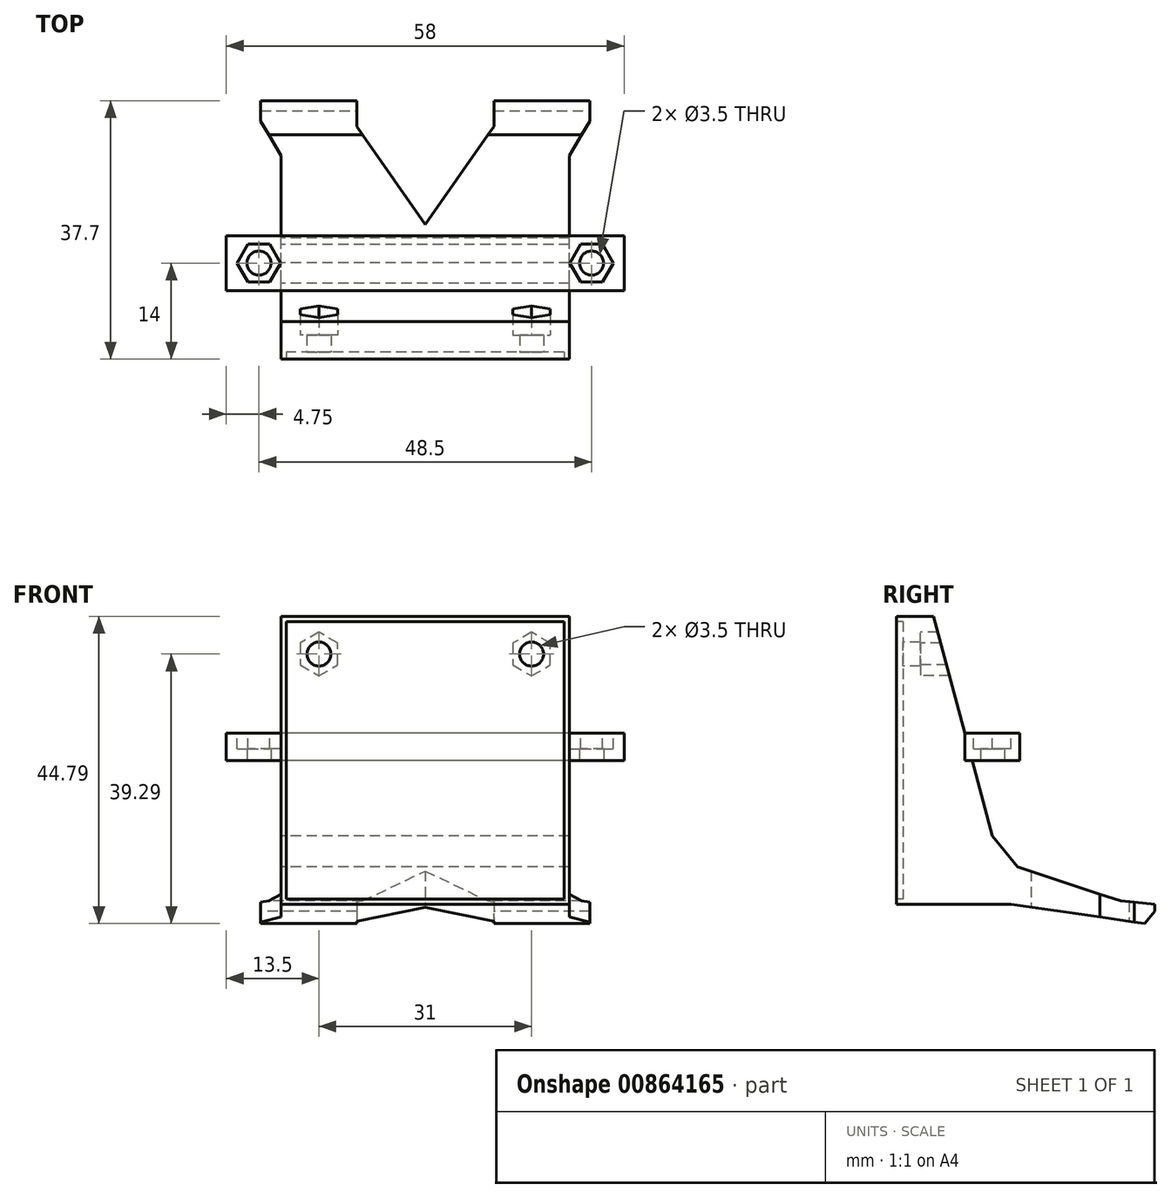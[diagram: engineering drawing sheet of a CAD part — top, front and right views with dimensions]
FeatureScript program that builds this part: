
annotation { "Feature Type Name" : "Feature", "Feature Type Description" : "" }
export const myFeature = defineFeature(function(context is Context, id is Id, definition is map)
    precondition{}
    {
        {
            var Q0;
            Q0=qCreatedBy(makeId("Top.planeOp"),FACE);
            var sketch = newSketch(context, id + "F0", { "sketchPlane" : qUnion([Q0])});
            skLineSegment(sketch, "E0", {"start": v(-24.25, 0) * mm, "end": v(0, 0) * mm, "construction": true});
            skLineSegment(sketch, "E1", {"start": v(0, 0) * mm, "end": v(24.25, 0) * mm, "construction": true});
            skCircle(sketch, "E2", {"center": v(-24.25, 0) * mm, "radius": 1.75 * mm});
            skCircle(sketch, "E3", {"center": v(24.25, 0) * mm, "radius": 1.75 * mm});
            skLineSegment(sketch, "E4.bottom", {"start": v(29, 4) * mm, "end": v(-29, 4) * mm});
            skLineSegment(sketch, "E4.top", {"start": v(29, -4) * mm, "end": v(-29, -4) * mm});
            skLineSegment(sketch, "E4.left", {"start": v(29, 4) * mm, "end": v(29, -4) * mm});
            skLineSegment(sketch, "E4.right", {"start": v(-29, 4) * mm, "end": v(-29, -4) * mm});
            skPoint(sketch, "E4.middle", {"position": v(0, 0) * mm});
            skSolve(sketch);
        }
        {
            var Q0;
            Q0 = qSketchRegion(id + "F0", true);
            extrude(context, id + "F1", {"entities" : qUnion([Q0]), "depth" : 4 * mm, "offsetDistance" : 25 * mm});
        }
        {
            var Q0;
            Q0=makeQuery(id+"F1.opExtrude","SWEPT_FACE",FACE,{"disambiguationData":[OSD([sQuery(id+"F0.wireOp",EDGE,"E4.top")])]});
            var sketch = newSketch(context, id + "F2", { "sketchPlane" : qUnion([Q0])});
            skLineSegment(sketch, "E5.bottom", {"start": v(21, 21) * mm, "end": v(-21, 21) * mm});
            skLineSegment(sketch, "E5.top", {"start": v(21, -21) * mm, "end": v(-21, -21) * mm});
            skLineSegment(sketch, "E5.left", {"start": v(21, 21) * mm, "end": v(21, -21) * mm});
            skLineSegment(sketch, "E5.right", {"start": v(-21, 21) * mm, "end": v(-21, -21) * mm});
            skLineSegment(sketch, "E6", {"start": v(-21, 0) * mm, "end": v(0, 0) * mm, "construction": true});
            skLineSegment(sketch, "E7", {"start": v(0, 0) * mm, "end": v(0, 21) * mm, "construction": true});
            skSolve(sketch);
        }
        {
            var Q0;
            Q0 = qSketchRegion(id + "F2", true);
            extrude(context, id + "F3", {"entities" : qUnion([Q0]), "operationType" : NewBodyOperationType.ADD, "depth" : 10 * mm, "offsetDistance" : 25 * mm});
        }
        {
            var Q0;
            Q0=makeQuery(id+"F1.opExtrude","CAP_FACE",FACE,{"disambiguationData":[OSD([sQuery(id+"F0.wireOp",EDGE,"E2"),sQuery(id+"F0.wireOp",EDGE,"E3"),sQuery(id+"F0.wireOp",EDGE,"E4.bottom"),sQuery(id+"F0.wireOp",EDGE,"E4.top"),sQuery(id+"F0.wireOp",EDGE,"E4.left"),sQuery(id+"F0.wireOp",EDGE,"E4.right")])],"isStart":false});
            var sketch = newSketch(context, id + "F4", { "sketchPlane" : qUnion([Q0])});
            skCircle(sketch, "E8.cCircle", {"center": v(24.25, 0) * mm, "radius": 2.75 * mm, "construction": true});
            skLineSegment(sketch, "E8.0", {"start": v(25.84, 2.75) * mm, "end": v(27.43, 0) * mm});
            skLineSegment(sketch, "E8.1", {"start": v(27.43, 0) * mm, "end": v(25.84, -2.75) * mm});
            skLineSegment(sketch, "E8.2", {"start": v(25.84, -2.75) * mm, "end": v(22.66, -2.75) * mm});
            skLineSegment(sketch, "E8.3", {"start": v(22.66, -2.75) * mm, "end": v(21.07, 0) * mm});
            skLineSegment(sketch, "E8.4", {"start": v(21.07, 0) * mm, "end": v(22.66, 2.75) * mm});
            skLineSegment(sketch, "E8.5", {"start": v(22.66, 2.75) * mm, "end": v(25.84, 2.75) * mm});
            skPoint(sketch, "E8.0.midPoint", {"position": v(26.63, 1.38) * mm});
            skCircle(sketch, "E9.cCircle", {"center": v(-24.25, 0) * mm, "radius": 2.75 * mm, "construction": true});
            skLineSegment(sketch, "E9.0", {"start": v(-21.07, 0) * mm, "end": v(-22.66, -2.75) * mm});
            skLineSegment(sketch, "E9.1", {"start": v(-22.66, -2.75) * mm, "end": v(-25.84, -2.75) * mm});
            skLineSegment(sketch, "E9.2", {"start": v(-25.84, -2.75) * mm, "end": v(-27.43, 0) * mm});
            skLineSegment(sketch, "E9.3", {"start": v(-27.43, 0) * mm, "end": v(-25.84, 2.75) * mm});
            skLineSegment(sketch, "E9.4", {"start": v(-25.84, 2.75) * mm, "end": v(-22.66, 2.75) * mm});
            skLineSegment(sketch, "E9.5", {"start": v(-22.66, 2.75) * mm, "end": v(-21.07, 0) * mm});
            skPoint(sketch, "E9.0.midPoint", {"position": v(-21.87, -1.38) * mm});
            skLineSegment(sketch, "E10", {"start": v(27.43, 0) * mm, "end": v(24.25, 0) * mm, "construction": true});
            skLineSegment(sketch, "E11", {"start": v(-21.07, 0) * mm, "end": v(-24.25, 0) * mm, "construction": true});
            skSolve(sketch);
        }
        {
            var Q0;
            Q0 = qSketchRegion(id + "F4", true);
            extrude(context, id + "F5", {"entities" : qUnion([Q0]), "operationType" : NewBodyOperationType.REMOVE, "oppositeDirection" : true, "depth" : 2.3 * mm, "offsetDistance" : 25 * mm});
        }
        {
            var Q0;
            Q0=makeQuery(id+"F3.opExtrude","SWEPT_FACE",FACE,{"disambiguationData":[OSD([sQuery(id+"F2.wireOp",EDGE,"E5.right")])]});
            var sketch = newSketch(context, id + "F6", { "sketchPlane" : qUnion([Q0])});
            skLineSegment(sketch, "E12", {"start": v(4, 21) * mm, "end": v(8.56, 21) * mm});
            skLineSegment(sketch, "E13", {"start": v(8.56, 21) * mm, "end": v(4, 4) * mm});
            skLineSegment(sketch, "E14", {"start": v(4, 4) * mm, "end": v(4, 21) * mm});
            skSolve(sketch);
        }
        {
            var Q0;
            Q0 = qSketchRegion(id + "F6", true);
            extrude(context, id + "F7", {"entities" : qUnion([Q0]), "operationType" : NewBodyOperationType.REMOVE, "endBound" : BoundingType.THROUGH_ALL, "oppositeDirection" : true, "depth" : 25 * mm, "offsetDistance" : 25 * mm});
        }
        {
            var Q0;
            Q0=makeQuery(id+"F3.opExtrude","SWEPT_FACE",FACE,{"disambiguationData":[OSD([sQuery(id+"F2.wireOp",EDGE,"E5.right")])]});
            var sketch = newSketch(context, id + "F8", { "sketchPlane" : qUnion([Q0])});
            skLineSegment(sketch, "E15", {"start": v(4, 0) * mm, "end": v(2.93, 0) * mm});
            skLineSegment(sketch, "E16", {"start": v(2.93, 0) * mm, "end": v(-2.7, -21) * mm});
            skLineSegment(sketch, "E17", {"start": v(-2.7, -21) * mm, "end": v(4, -21) * mm});
            skLineSegment(sketch, "E18", {"start": v(4, -21) * mm, "end": v(4, 0) * mm});
            skSolve(sketch);
        }
        {
            var Q0;
            Q0 = qSketchRegion(id + "F8", true);
            var Q1;
            Q1=makeQuery(id+"F3.opExtrude","SWEPT_FACE",FACE,{"disambiguationData":[OSD([sQuery(id+"F2.wireOp",EDGE,"E5.left")])]});
            extrude(context, id + "F9", {"entities" : qUnion([Q0]), "operationType" : NewBodyOperationType.ADD, "endBound" : BoundingType.UP_TO_SURFACE, "oppositeDirection" : true, "depth" : 25 * mm, "endBoundEntityFace" : qUnion([Q1]), "offsetDistance" : 25 * mm});
        }
        {
            var Q0;
            Q0=makeQuery(id+"F3.opExtrude","CAP_FACE",FACE,{"disambiguationData":[OSD([sQuery(id+"F2.wireOp",EDGE,"E5.bottom"),sQuery(id+"F2.wireOp",EDGE,"E5.top"),sQuery(id+"F2.wireOp",EDGE,"E5.left"),sQuery(id+"F2.wireOp",EDGE,"E5.right")])],"isStart":false});
            var sketch = newSketch(context, id + "F10", { "sketchPlane" : qUnion([Q0])});
            skLineSegment(sketch, "E19.bottom", {"start": v(15.5, -15.5) * mm, "end": v(-15.5, -15.5) * mm, "construction": true});
            skLineSegment(sketch, "E19.top", {"start": v(15.5, 15.5) * mm, "end": v(-15.5, 15.5) * mm, "construction": true});
            skLineSegment(sketch, "E19.left", {"start": v(15.5, -15.5) * mm, "end": v(15.5, 15.5) * mm, "construction": true});
            skLineSegment(sketch, "E19.right", {"start": v(-15.5, -15.5) * mm, "end": v(-15.5, 15.5) * mm, "construction": true});
            skPoint(sketch, "E19.middle", {"position": v(0, 0) * mm});
            skCircle(sketch, "E20", {"center": v(-15.5, 15.5) * mm, "radius": 1.75 * mm});
            skCircle(sketch, "E21", {"center": v(15.5, 15.5) * mm, "radius": 1.75 * mm});
            skSolve(sketch);
        }
        {
            var Q0;
            Q0 = qSketchRegion(id + "F10", true);
            extrude(context, id + "F11", {"entities" : qUnion([Q0]), "operationType" : NewBodyOperationType.REMOVE, "oppositeDirection" : true, "depth" : 25 * mm, "offsetDistance" : 25 * mm});
        }
        {
            var Q0;
            Q0=makeQuery(id+"F9.boolean.opBoolean","MERGE",FACE,{"derivedFrom":[makeQuery(id+"F3.opExtrude","SWEPT_FACE",FACE,{"disambiguationData":[OSD([sQuery(id+"F2.wireOp",EDGE,"E5.right")])]}),makeQuery(id+"F9.opExtrude","CAP_FACE",FACE,{"disambiguationData":[OSD([sQuery(id+"F8.wireOp",EDGE,"E15"),sQuery(id+"F8.wireOp",EDGE,"E16"),sQuery(id+"F8.wireOp",EDGE,"E17"),sQuery(id+"F8.wireOp",EDGE,"E18")])],"isStart":true})]});
            var sketch = newSketch(context, id + "F12", { "sketchPlane" : qUnion([Q0])});
            skLineSegment(sketch, "E22", {"start": v(-2.7, -21) * mm, "end": v(-23.7, -24) * mm});
            skLineSegment(sketch, "E23", {"start": v(-23.7, -24) * mm, "end": v(-23.7, -21) * mm});
            skLineSegment(sketch, "E24", {"start": v(-0.02, -11) * mm, "end": v(-2.7, -21) * mm});
            skLineSegment(sketch, "E25", {"start": v(-0.02, -11) * mm, "end": v(-3.7, -15.5) * mm});
            skLineSegment(sketch, "E26", {"start": v(-3.7, -15.5) * mm, "end": v(-18.7, -20.5) * mm});
            skLineSegment(sketch, "E27", {"start": v(-18.7, -20.5) * mm, "end": v(-23.7, -21) * mm});
            skSolve(sketch);
        }
        {
            var Q0;
            Q0 = qSketchRegion(id + "F12", true);
            var Q1;
            Q1=makeQuery(id+"F9.boolean.opBoolean","MERGE",FACE,{"derivedFrom":[makeQuery(id+"F3.opExtrude","SWEPT_FACE",FACE,{"disambiguationData":[OSD([sQuery(id+"F2.wireOp",EDGE,"E5.left")])]}),makeQuery(id+"F9.opExtrude","CAP_FACE",FACE,{"disambiguationData":[OSD([sQuery(id+"F8.wireOp",EDGE,"E15"),sQuery(id+"F8.wireOp",EDGE,"E16"),sQuery(id+"F8.wireOp",EDGE,"E17"),sQuery(id+"F8.wireOp",EDGE,"E18")])],"isStart":false})]});
            extrude(context, id + "F13", {"entities" : qUnion([Q0]), "operationType" : NewBodyOperationType.ADD, "endBound" : BoundingType.UP_TO_SURFACE, "oppositeDirection" : true, "depth" : 25 * mm, "endBoundEntityFace" : qUnion([Q1]), "offsetDistance" : 25 * mm});
        }
        {
            var Q0;
            Q0=makeQuery(id+"F3.opExtrude","CAP_FACE",FACE,{"disambiguationData":[OSD([sQuery(id+"F2.wireOp",EDGE,"E5.bottom"),sQuery(id+"F2.wireOp",EDGE,"E5.top"),sQuery(id+"F2.wireOp",EDGE,"E5.left"),sQuery(id+"F2.wireOp",EDGE,"E5.right")])],"isStart":false});
            var sketch = newSketch(context, id + "F14", { "sketchPlane" : qUnion([Q0])});
            skLineSegment(sketch, "E28.bottom", {"start": v(20.25, 20.25) * mm, "end": v(-20.25, 20.25) * mm});
            skLineSegment(sketch, "E28.top", {"start": v(20.25, -20.25) * mm, "end": v(-20.25, -20.25) * mm});
            skLineSegment(sketch, "E28.left", {"start": v(20.25, 20.25) * mm, "end": v(20.25, -20.25) * mm});
            skLineSegment(sketch, "E28.right", {"start": v(-20.25, 20.25) * mm, "end": v(-20.25, -20.25) * mm});
            skPoint(sketch, "E28.middle", {"position": v(0, 0) * mm});
            skSolve(sketch);
        }
        {
            var Q0;
            Q0 = qSketchRegion(id + "F14", true);
            extrude(context, id + "F15", {"entities" : qUnion([Q0]), "operationType" : NewBodyOperationType.REMOVE, "oppositeDirection" : true, "depth" : 1 * mm, "offsetDistance" : 25 * mm});
        }
        {
            var Q0;
            Q0=makeQuery(id+"F13.opExtrude","SWEPT_EDGE",EDGE,{"disambiguationData":[OSD([sQuery(id+"F12.wireOp",EDGE,"E22"),sQuery(id+"F12.wireOp",EDGE,"E23")])]});
            chamfer(context, id + "F16", {"entities" : qUnion([Q0]), "chamferType" : ChamferType.TWO_OFFSETS, "width1" : 2 * mm, "oppositeDirection" : false, "width2" : 1.5 * mm, "tangentPropagation" : true});
        }
        {
            var Q0;
            Q0=makeQuery(id+"F13.boolean.opBoolean","MERGE",FACE,{"derivedFrom":[makeQuery(id+"F9.boolean.opBoolean","MERGE",FACE,{"derivedFrom":[makeQuery(id+"F3.opExtrude","SWEPT_FACE",FACE,{"disambiguationData":[OSD([sQuery(id+"F2.wireOp",EDGE,"E5.right")])]}),makeQuery(id+"F9.opExtrude","CAP_FACE",FACE,{"disambiguationData":[OSD([sQuery(id+"F8.wireOp",EDGE,"E15"),sQuery(id+"F8.wireOp",EDGE,"E16"),sQuery(id+"F8.wireOp",EDGE,"E17"),sQuery(id+"F8.wireOp",EDGE,"E18")])],"isStart":true})]}),makeQuery(id+"F13.opExtrude","CAP_FACE",FACE,{"disambiguationData":[OSD([sQuery(id+"F12.wireOp",EDGE,"E22"),sQuery(id+"F12.wireOp",EDGE,"E23"),sQuery(id+"F12.wireOp",EDGE,"E24"),sQuery(id+"F12.wireOp",EDGE,"E25"),sQuery(id+"F12.wireOp",EDGE,"OhSGq7lQ-fsdC-TyxC-lwQv-2I8dridQHh3y")])],"isStart":true})]});
            var sketch = newSketch(context, id + "F17", { "sketchPlane" : qUnion([Q0])});
            skLineSegment(sketch, "E29.0", {"start": v(-23.7, -22) * mm, "end": v(-22.21, -23.79) * mm});
            skLineSegment(sketch, "E29.1", {"start": v(-23.7, -22) * mm, "end": v(-23.7, -21) * mm});
            skLineSegment(sketch, "E30", {"start": v(-15.7, -19.5) * mm, "end": v(-15.7, -22.86) * mm});
            skLineSegment(sketch, "E31", {"start": v(-15.7, -22.86) * mm, "end": v(-22.21, -23.79) * mm});
            skLineSegment(sketch, "E32.0", {"start": v(-18.7, -20.5) * mm, "end": v(-23.7, -21) * mm});
            skLineSegment(sketch, "E32.1", {"start": v(-15.7, -19.5) * mm, "end": v(-18.7, -20.5) * mm});
            skPoint(sketch, "E33.orphan", {"position": v(-3.7, -15.5) * mm});
            skSolve(sketch);
        }
        {
            var Q0;
            Q0 = qSketchRegion(id + "F17", true);
            extrude(context, id + "F18", {"entities" : qUnion([Q0]), "operationType" : NewBodyOperationType.ADD, "depth" : 3 * mm, "offsetDistance" : 25 * mm});
        }
        {
            var Q0;
            Q0=makeQuery(id+"F13.boolean.opBoolean","MERGE",FACE,{"derivedFrom":[makeQuery(id+"F9.boolean.opBoolean","MERGE",FACE,{"derivedFrom":[makeQuery(id+"F3.opExtrude","SWEPT_FACE",FACE,{"disambiguationData":[OSD([sQuery(id+"F2.wireOp",EDGE,"E5.left")])]}),makeQuery(id+"F9.opExtrude","CAP_FACE",FACE,{"disambiguationData":[OSD([sQuery(id+"F8.wireOp",EDGE,"E15"),sQuery(id+"F8.wireOp",EDGE,"E16"),sQuery(id+"F8.wireOp",EDGE,"E17"),sQuery(id+"F8.wireOp",EDGE,"E18")])],"isStart":false})]}),makeQuery(id+"F13.opExtrude","CAP_FACE",FACE,{"disambiguationData":[OSD([sQuery(id+"F12.wireOp",EDGE,"E22"),sQuery(id+"F12.wireOp",EDGE,"E23"),sQuery(id+"F12.wireOp",EDGE,"E24"),sQuery(id+"F12.wireOp",EDGE,"E25"),sQuery(id+"F12.wireOp",EDGE,"OhSGq7lQ-fsdC-TyxC-lwQv-2I8dridQHh3y")])],"isStart":false})]});
            var sketch = newSketch(context, id + "F19", { "sketchPlane" : qUnion([Q0])});
            skLineSegment(sketch, "E34.0", {"start": v(22.21, -23.79) * mm, "end": v(23.7, -22) * mm});
            skLineSegment(sketch, "E34.1", {"start": v(23.7, -22) * mm, "end": v(23.7, -21) * mm});
            skLineSegment(sketch, "E35", {"start": v(22.21, -23.79) * mm, "end": v(15.7, -22.86) * mm});
            skLineSegment(sketch, "E36", {"start": v(15.7, -22.86) * mm, "end": v(15.7, -19.5) * mm});
            skLineSegment(sketch, "E37.0", {"start": v(18.7, -20.5) * mm, "end": v(23.7, -21) * mm});
            skLineSegment(sketch, "E37.1", {"start": v(15.7, -19.5) * mm, "end": v(18.7, -20.5) * mm});
            skPoint(sketch, "E38.orphan", {"position": v(3.7, -15.5) * mm});
            skSolve(sketch);
        }
        {
            var Q0;
            Q0 = qSketchRegion(id + "F19", true);
            extrude(context, id + "F20", {"entities" : qUnion([Q0]), "operationType" : NewBodyOperationType.ADD, "depth" : 3 * mm, "offsetDistance" : 25 * mm});
        }
        {
            var Q0;
            Q0=makeQuery(id+"F20.opExtrude","CAP_EDGE",EDGE,{"disambiguationData":[OSD([sQuery(id+"F19.wireOp",EDGE,"E36")])],"isStart":false});
            var Q1;
            Q1=makeQuery(id+"F18.opExtrude","CAP_EDGE",EDGE,{"disambiguationData":[OSD([sQuery(id+"F17.wireOp",EDGE,"E30")])],"isStart":false});
            chamfer(context, id + "F21", {"entities" : qUnion([Q0, Q1]), "chamferType" : ChamferType.TWO_OFFSETS, "width1" : 3 * mm, "oppositeDirection" : false, "width2" : 5 * mm, "tangentPropagation" : true});
        }
        {
            var Q0;
            Q0=makeQuery(id+"F15.boolean.opBoolean","COPY",FACE,{"derivedFrom":makeQuery(id+"F15.opExtrude","CAP_FACE",FACE,{"disambiguationData":[OSD([sQuery(id+"F14.wireOp",EDGE,"E28.bottom"),sQuery(id+"F14.wireOp",EDGE,"E28.top"),sQuery(id+"F14.wireOp",EDGE,"E28.left"),sQuery(id+"F14.wireOp",EDGE,"E28.right")])],"isStart":false})});
            cPlane(context, id + "F22", {"entities" : qUnion([Q0]), "cplaneType" : CPlaneType.OFFSET, "offset" : 2.5 * mm, "oppositeDirection" : true, "width" : 150 * mm, "height" : 150 * mm});
        }
        {
            var Q0;
            Q0=qCreatedBy(id+"F22.planeOp",FACE);
            var sketch = newSketch(context, id + "F23", { "sketchPlane" : qUnion([Q0])});
            skCircle(sketch, "E39.cCircle", {"center": v(15.5, 15.5) * mm, "radius": 2.75 * mm, "construction": true});
            skLineSegment(sketch, "E39.0", {"start": v(12.75, 13.91) * mm, "end": v(12.75, 17.09) * mm});
            skLineSegment(sketch, "E39.1", {"start": v(12.75, 17.09) * mm, "end": v(15.5, 18.68) * mm});
            skLineSegment(sketch, "E39.2", {"start": v(15.5, 18.68) * mm, "end": v(18.25, 17.09) * mm});
            skLineSegment(sketch, "E39.3", {"start": v(18.25, 17.09) * mm, "end": v(18.25, 13.91) * mm});
            skLineSegment(sketch, "E39.4", {"start": v(18.25, 13.91) * mm, "end": v(15.5, 12.32) * mm});
            skLineSegment(sketch, "E39.5", {"start": v(15.5, 12.32) * mm, "end": v(12.75, 13.91) * mm});
            skPoint(sketch, "E39.0.midPoint", {"position": v(12.75, 15.5) * mm});
            skCircle(sketch, "E40.cCircle", {"center": v(-15.5, 15.5) * mm, "radius": 2.75 * mm, "construction": true});
            skLineSegment(sketch, "E40.0", {"start": v(-12.75, 17.09) * mm, "end": v(-12.75, 13.91) * mm});
            skLineSegment(sketch, "E40.1", {"start": v(-12.75, 13.91) * mm, "end": v(-15.5, 12.32) * mm});
            skLineSegment(sketch, "E40.2", {"start": v(-15.5, 12.32) * mm, "end": v(-18.25, 13.91) * mm});
            skLineSegment(sketch, "E40.3", {"start": v(-18.25, 13.91) * mm, "end": v(-18.25, 17.09) * mm});
            skLineSegment(sketch, "E40.4", {"start": v(-18.25, 17.09) * mm, "end": v(-15.5, 18.68) * mm});
            skLineSegment(sketch, "E40.5", {"start": v(-15.5, 18.68) * mm, "end": v(-12.75, 17.09) * mm});
            skPoint(sketch, "E40.0.midPoint", {"position": v(-12.75, 15.5) * mm});
            skLineSegment(sketch, "E41", {"start": v(15.5, 18.68) * mm, "end": v(15.5, 15.5) * mm, "construction": true});
            skLineSegment(sketch, "E42", {"start": v(-15.5, 18.68) * mm, "end": v(-15.5, 15.5) * mm, "construction": true});
            skSolve(sketch);
        }
        {
            var Q0;
            Q0 = qSketchRegion(id + "F23", true);
            extrude(context, id + "F24", {"entities" : qUnion([Q0]), "operationType" : NewBodyOperationType.REMOVE, "oppositeDirection" : true, "depth" : 25 * mm, "offsetDistance" : 25 * mm});
        }
        {
            var Q0;
            Q0=makeQuery(id+"F9.boolean.opBoolean","MERGE",FACE,{"derivedFrom":[makeQuery(id+"F3.opExtrude","SWEPT_FACE",FACE,{"disambiguationData":[OSD([sQuery(id+"F2.wireOp",EDGE,"E5.top")])]}),makeQuery(id+"F9.opExtrude","SWEPT_FACE",FACE,{"disambiguationData":[OSD([sQuery(id+"F8.wireOp",EDGE,"E17")])]})]});
            var sketch = newSketch(context, id + "F25", { "sketchPlane" : qUnion([Q0])});
            skLineSegment(sketch, "E43", {"start": v(10, -23.7) * mm, "end": v(10, -19.9) * mm});
            skLineSegment(sketch, "E44", {"start": v(10, -19.9) * mm, "end": v(0, -5.62) * mm});
            skLineSegment(sketch, "E45", {"start": v(0, -5.62) * mm, "end": v(-10, -19.9) * mm});
            skLineSegment(sketch, "E46", {"start": v(-10, -19.9) * mm, "end": v(-10, -23.7) * mm});
            skLineSegment(sketch, "E47", {"start": v(-10, -23.7) * mm, "end": v(10, -23.7) * mm});
            skLineSegment(sketch, "E48", {"start": v(0, -5.62) * mm, "end": v(0, -23.7) * mm, "construction": true});
            skLineSegment(sketch, "E49", {"start": v(0, 0) * mm, "end": v(0, -5.62) * mm, "construction": true});
            skSolve(sketch);
        }
        {
            var Q0;
            Q0 = qSketchRegion(id + "F25", true);
            extrude(context, id + "F26", {"entities" : qUnion([Q0]), "operationType" : NewBodyOperationType.REMOVE, "endBound" : BoundingType.SYMMETRIC, "oppositeDirection" : true, "depth" : 10 * mm, "offsetDistance" : 25 * mm});
        }
    });
